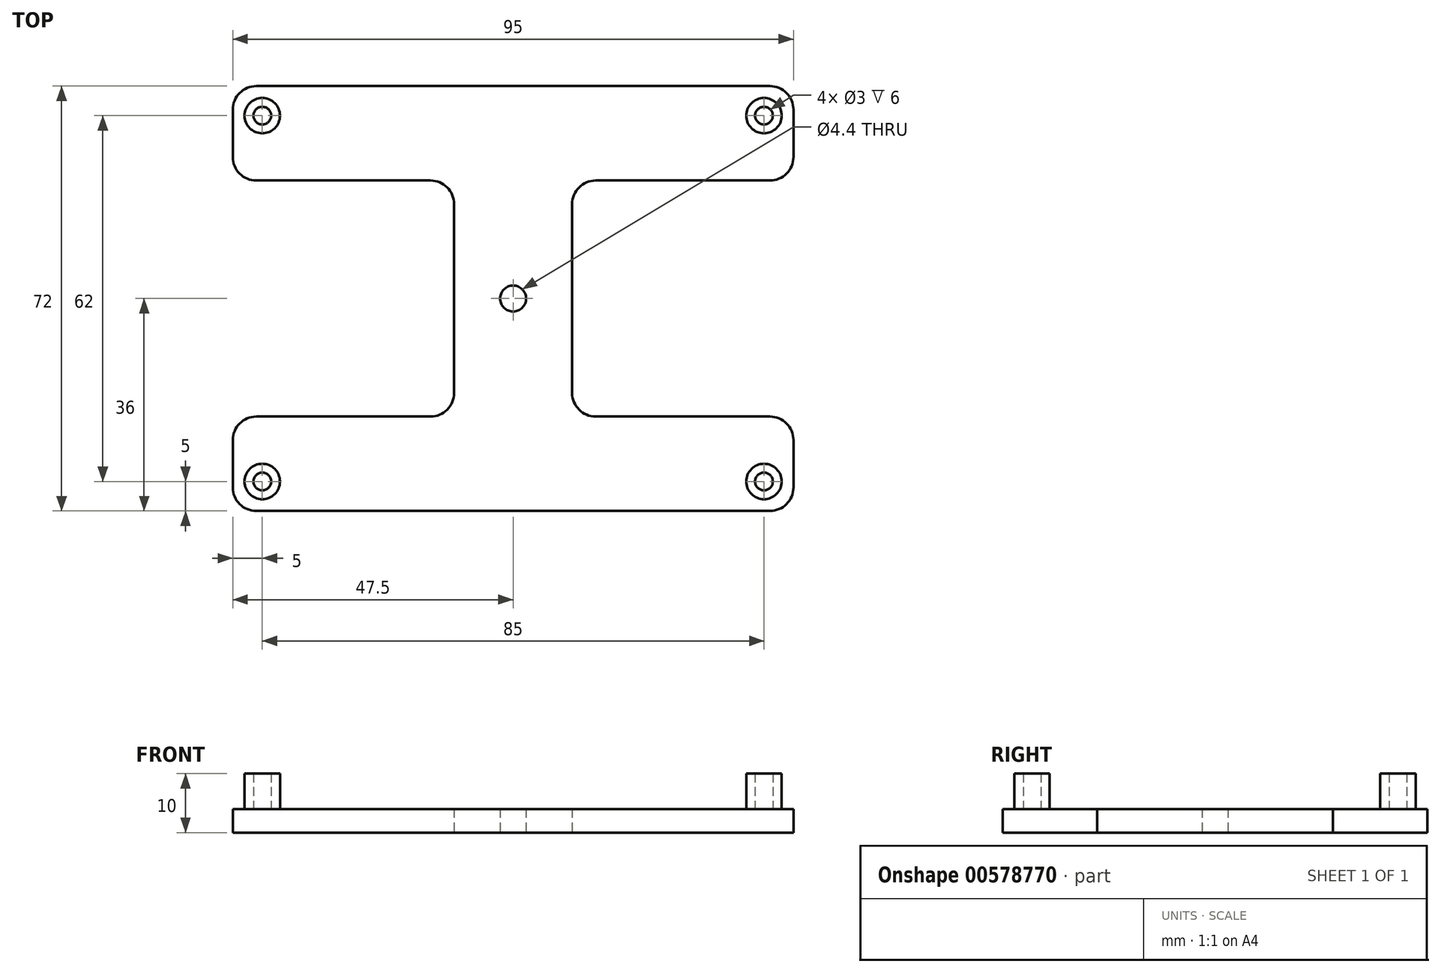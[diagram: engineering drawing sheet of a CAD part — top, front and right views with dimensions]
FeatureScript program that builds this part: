
annotation { "Feature Type Name" : "Feature", "Feature Type Description" : "" }
export const myFeature = defineFeature(function(context is Context, id is Id, definition is map)
    precondition{}
    {
        {
            var Q0;
            Q0=qCreatedBy(makeId("Top.planeOp"),FACE);
            var sketch = newSketch(context, id + "F0", { "sketchPlane" : qUnion([Q0])});
            skLineSegment(sketch, "E0.bottom", {"start": v(43.5, 36) * mm, "end": v(-43.5, 36) * mm});
            skLineSegment(sketch, "E0.top", {"start": v(43.5, -36) * mm, "end": v(-43.5, -36) * mm});
            skLineSegment(sketch, "E0.left", {"start": v(47.5, 32) * mm, "end": v(47.5, 24) * mm});
            skLineSegment(sketch, "E0.right", {"start": v(-47.5, 32) * mm, "end": v(-47.5, 24) * mm});
            skPoint(sketch, "E0.middle", {"position": v(0, 0) * mm});
            skPoint(sketch, "E1.visualSharp", {"position": v(-47.5, 36) * mm});
            skArc(sketch, "E1.filletArc", {"start": v(-43.5, 36) * mm, "mid": v(-46.33, 34.83) * mm, "end": v(-47.5, 32) * mm});
            skPoint(sketch, "E2.visualSharp", {"position": v(47.5, 36) * mm});
            skArc(sketch, "E2.filletArc", {"start": v(47.5, 32) * mm, "mid": v(46.33, 34.83) * mm, "end": v(43.5, 36) * mm});
            skPoint(sketch, "E3.visualSharp", {"position": v(47.5, -36) * mm});
            skArc(sketch, "E3.filletArc", {"start": v(43.5, -36) * mm, "mid": v(46.33, -34.83) * mm, "end": v(47.5, -32) * mm});
            skPoint(sketch, "E4.visualSharp", {"position": v(-47.5, -36) * mm});
            skArc(sketch, "E4.filletArc", {"start": v(-47.5, -32) * mm, "mid": v(-46.33, -34.83) * mm, "end": v(-43.5, -36) * mm});
            skCircle(sketch, "E5", {"center": v(0, 0) * mm, "radius": 2.2 * mm});
            skLineSegment(sketch, "E6.bottom", {"start": v(-43.5, 20) * mm, "end": v(-14, 20) * mm});
            skLineSegment(sketch, "E6.top", {"start": v(-43.5, -20) * mm, "end": v(-14, -20) * mm});
            skLineSegment(sketch, "E6.right", {"start": v(-10, 16) * mm, "end": v(-10, -16) * mm});
            skLineSegment(sketch, "E7.bottom", {"start": v(43.5, 20) * mm, "end": v(14, 20) * mm});
            skLineSegment(sketch, "E7.top", {"start": v(43.5, -20) * mm, "end": v(14, -20) * mm});
            skLineSegment(sketch, "E7.right", {"start": v(10, 16) * mm, "end": v(10, -16) * mm});
            skLineSegment(sketch, "E8.trimOffspring", {"start": v(-47.5, -24) * mm, "end": v(-47.5, -32) * mm});
            skLineSegment(sketch, "E9.trimOffspring", {"start": v(47.5, -24) * mm, "end": v(47.5, -32) * mm});
            skPoint(sketch, "E10.visualSharp", {"position": v(-47.5, 20) * mm});
            skArc(sketch, "E10.filletArc", {"start": v(-47.5, 24) * mm, "mid": v(-46.33, 21.17) * mm, "end": v(-43.5, 20) * mm});
            skPoint(sketch, "E11.visualSharp", {"position": v(-10, 20) * mm});
            skArc(sketch, "E11.filletArc", {"start": v(-10, 16) * mm, "mid": v(-11.17, 18.83) * mm, "end": v(-14, 20) * mm});
            skPoint(sketch, "E12.visualSharp", {"position": v(10, 20) * mm});
            skArc(sketch, "E12.filletArc", {"start": v(14, 20) * mm, "mid": v(11.17, 18.83) * mm, "end": v(10, 16) * mm});
            skPoint(sketch, "E13.visualSharp", {"position": v(47.5, 20) * mm});
            skArc(sketch, "E13.filletArc", {"start": v(43.5, 20) * mm, "mid": v(46.33, 21.17) * mm, "end": v(47.5, 24) * mm});
            skPoint(sketch, "E14.visualSharp", {"position": v(10, -20) * mm});
            skArc(sketch, "E14.filletArc", {"start": v(10, -16) * mm, "mid": v(11.17, -18.83) * mm, "end": v(14, -20) * mm});
            skPoint(sketch, "E15.visualSharp", {"position": v(47.5, -20) * mm});
            skArc(sketch, "E15.filletArc", {"start": v(47.5, -24) * mm, "mid": v(46.33, -21.17) * mm, "end": v(43.5, -20) * mm});
            skPoint(sketch, "E16.visualSharp", {"position": v(-10, -20) * mm});
            skArc(sketch, "E16.filletArc", {"start": v(-14, -20) * mm, "mid": v(-11.17, -18.83) * mm, "end": v(-10, -16) * mm});
            skPoint(sketch, "E17.visualSharp", {"position": v(-47.5, -20) * mm});
            skArc(sketch, "E17.filletArc", {"start": v(-43.5, -20) * mm, "mid": v(-46.33, -21.17) * mm, "end": v(-47.5, -24) * mm});
            skSolve(sketch);
        }
        {
            var Q0;
            Q0=makeQuery(id+"F0.imprint","IMPRINT",FACE,{"disambiguationData":[TD([[makeQuery(id+"F0.imprint","IMPRINT",EDGE,{"derivedFrom":sQuery(id+"F0.wireOp",EDGE,"E0.bottom")}),1.0]])]});
            extrude(context, id + "F1", {"entities" : qUnion([Q0]), "depth" : 4 * mm, "offsetDistance" : 25 * mm});
        }
        {
            var Q0;
            Q0=makeQuery(id+"F1.opExtrude","CAP_FACE",FACE,{"disambiguationData":[OSD([sQuery(id+"F0.wireOp",EDGE,"E0.bottom"),sQuery(id+"F0.wireOp",EDGE,"E0.top"),sQuery(id+"F0.wireOp",EDGE,"E0.left"),sQuery(id+"F0.wireOp",EDGE,"E0.right")])],"isStart":false});
            var sketch = newSketch(context, id + "F2", { "sketchPlane" : qUnion([Q0])});
            skCircle(sketch, "E18", {"center": v(-42.5, 31) * mm, "radius": 3 * mm});
            skCircle(sketch, "E19", {"center": v(42.5, 31) * mm, "radius": 3 * mm});
            skCircle(sketch, "E20", {"center": v(42.5, -31) * mm, "radius": 3 * mm});
            skCircle(sketch, "E21", {"center": v(-42.5, -31) * mm, "radius": 3 * mm});
            skCircle(sketch, "E22", {"center": v(-42.5, 31) * mm, "radius": 1.5 * mm});
            skCircle(sketch, "E23", {"center": v(42.5, 31) * mm, "radius": 1.5 * mm});
            skCircle(sketch, "E24", {"center": v(42.5, -31) * mm, "radius": 1.5 * mm});
            skCircle(sketch, "E25", {"center": v(-42.5, -31) * mm, "radius": 1.5 * mm});
            skSolve(sketch);
        }
        {
            var Q0;
            Q0 = qSketchRegion(id + "F2", true);
            extrude(context, id + "F3", {"entities" : qUnion([Q0]), "operationType" : NewBodyOperationType.ADD, "depth" : 6 * mm, "offsetDistance" : 25 * mm});
        }
    });
